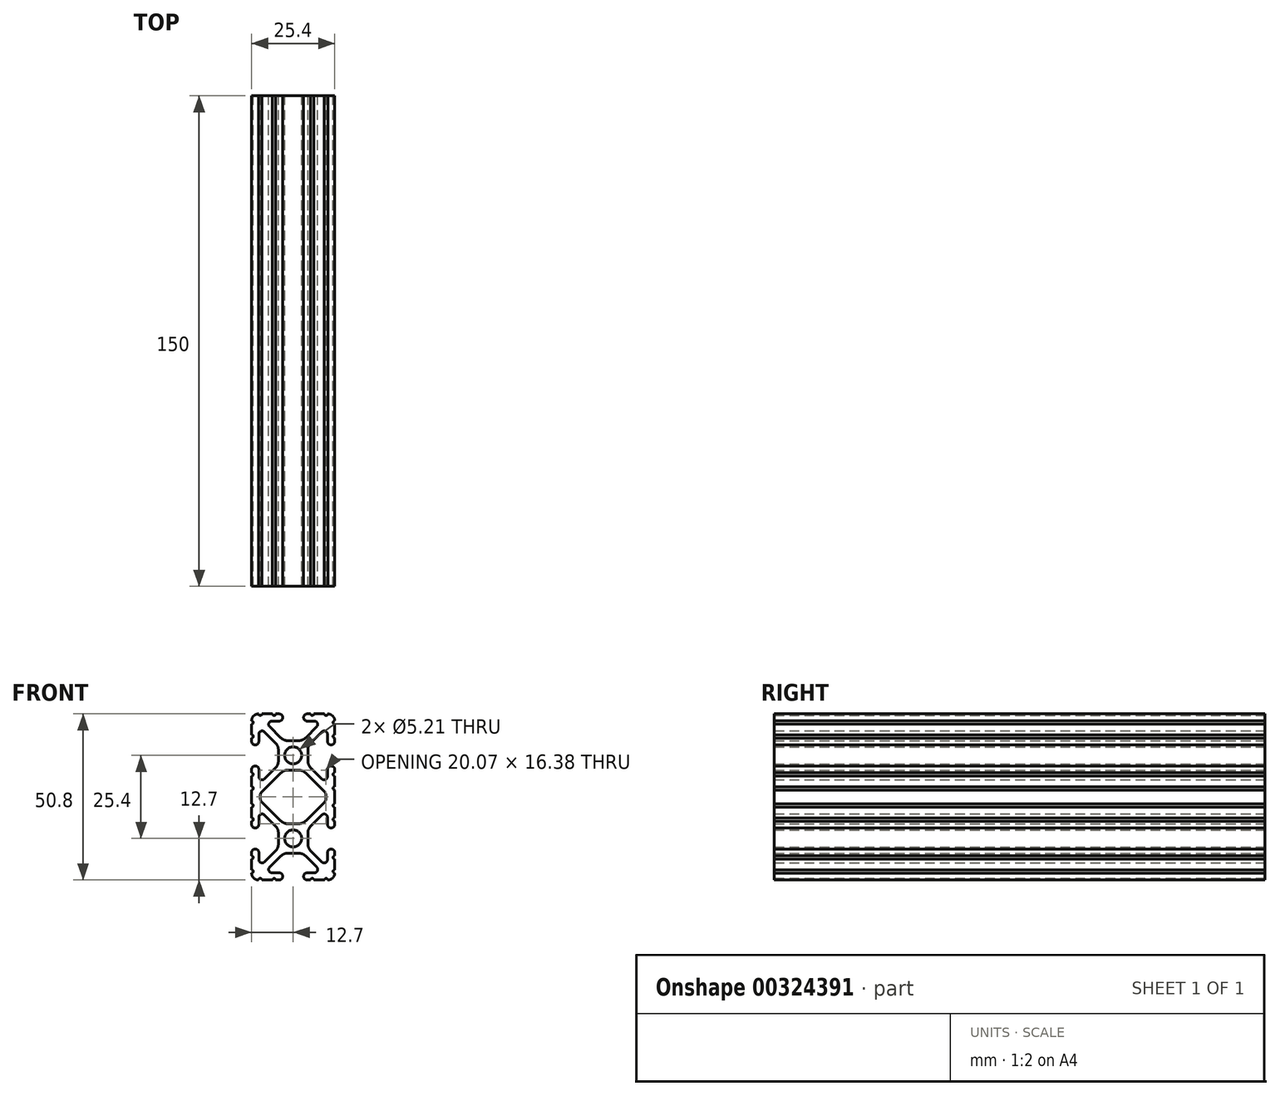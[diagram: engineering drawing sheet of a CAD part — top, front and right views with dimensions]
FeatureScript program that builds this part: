
annotation { "Feature Type Name" : "Feature", "Feature Type Description" : "" }
export const myFeature = defineFeature(function(context is Context, id is Id, definition is map)
    precondition{}
    {
        {
            var Q0;
            Q0=qCreatedBy(makeId("Front.planeOp"),FACE);
            var sketch = newSketch(context, id + "F0", { "sketchPlane" : qUnion([Q0])});
            skArc(sketch, "E0", {"start": v(2.6, -12.7) * mm, "mid": v(0, -10.1) * mm, "end": v(-2.6, -12.7) * mm});
            skArc(sketch, "E1", {"start": v(-2.6, -12.7) * mm, "mid": v(0, -15.3) * mm, "end": v(2.6, -12.7) * mm});
            skArc(sketch, "E2", {"start": v(-12.7, 22.25) * mm, "mid": v(-12.2, 22.76) * mm, "end": v(-12.7, 23.28) * mm});
            skLineSegment(sketch, "E3", {"start": v(-12.7, 22.25) * mm, "end": v(-12.7, 19.02) * mm});
            skArc(sketch, "E4", {"start": v(-12.7, 18) * mm, "mid": v(-12.2, 18.52) * mm, "end": v(-12.7, 19.02) * mm});
            skLineSegment(sketch, "E5", {"start": v(-12.7, 18) * mm, "end": v(-12.7, 17) * mm});
            skArc(sketch, "E6", {"start": v(-12.7, 17) * mm, "mid": v(-11.6, 15.9) * mm, "end": v(-10.5, 17) * mm});
            skLineSegment(sketch, "E7", {"start": v(-10.5, 17) * mm, "end": v(-10.5, 19.17) * mm});
            skArc(sketch, "E8", {"start": v(-8.76, 19.9) * mm, "mid": v(-9.86, 20.11) * mm, "end": v(-10.5, 19.17) * mm});
            skLineSegment(sketch, "E9", {"start": v(-8.76, 19.9) * mm, "end": v(-5.44, 16.58) * mm});
            skArc(sketch, "E10", {"start": v(-4.5, 14.33) * mm, "mid": v(-4.75, 15.55) * mm, "end": v(-5.44, 16.58) * mm});
            skLineSegment(sketch, "E11", {"start": v(-4.5, 14.33) * mm, "end": v(-4.5, 11.07) * mm});
            skArc(sketch, "E12", {"start": v(-5.44, 8.82) * mm, "mid": v(-4.75, 9.85) * mm, "end": v(-4.5, 11.07) * mm});
            skLineSegment(sketch, "E13", {"start": v(-5.44, 8.82) * mm, "end": v(-8.76, 5.5) * mm});
            skArc(sketch, "E14", {"start": v(-10.5, 6.23) * mm, "mid": v(-9.86, 5.29) * mm, "end": v(-8.76, 5.5) * mm});
            skLineSegment(sketch, "E15", {"start": v(-10.5, 6.23) * mm, "end": v(-10.5, 8.4) * mm});
            skArc(sketch, "E16", {"start": v(-10.5, 8.4) * mm, "mid": v(-11.6, 9.5) * mm, "end": v(-12.7, 8.4) * mm});
            skLineSegment(sketch, "E17", {"start": v(-12.7, 8.4) * mm, "end": v(-12.7, 7.4) * mm});
            skArc(sketch, "E18", {"start": v(-12.7, 6.38) * mm, "mid": v(-12.2, 6.88) * mm, "end": v(-12.7, 7.4) * mm});
            skLineSegment(sketch, "E19", {"start": v(-12.7, 6.38) * mm, "end": v(-12.7, 3.15) * mm});
            skArc(sketch, "E20", {"start": v(-12.7, 2.13) * mm, "mid": v(-12.2, 2.64) * mm, "end": v(-12.7, 3.15) * mm});
            skLineSegment(sketch, "E21", {"start": v(-12.7, 2.13) * mm, "end": v(-12.7, -2.13) * mm});
            skArc(sketch, "E22", {"start": v(-12.7, -3.15) * mm, "mid": v(-12.2, -2.64) * mm, "end": v(-12.7, -2.13) * mm});
            skLineSegment(sketch, "E23", {"start": v(-12.7, -3.15) * mm, "end": v(-12.7, -6.38) * mm});
            skArc(sketch, "E24", {"start": v(-12.7, -7.4) * mm, "mid": v(-12.2, -6.88) * mm, "end": v(-12.7, -6.38) * mm});
            skLineSegment(sketch, "E25", {"start": v(-12.7, -7.4) * mm, "end": v(-12.7, -8.4) * mm});
            skArc(sketch, "E26", {"start": v(-12.7, -8.4) * mm, "mid": v(-11.6, -9.5) * mm, "end": v(-10.5, -8.4) * mm});
            skLineSegment(sketch, "E27", {"start": v(-10.5, -8.4) * mm, "end": v(-10.5, -6.23) * mm});
            skArc(sketch, "E28", {"start": v(-8.76, -5.5) * mm, "mid": v(-9.86, -5.29) * mm, "end": v(-10.5, -6.23) * mm});
            skLineSegment(sketch, "E29", {"start": v(-8.76, -5.5) * mm, "end": v(-5.44, -8.82) * mm});
            skArc(sketch, "E30", {"start": v(-4.5, -11.07) * mm, "mid": v(-4.75, -9.85) * mm, "end": v(-5.44, -8.82) * mm});
            skLineSegment(sketch, "E31", {"start": v(-4.5, -11.07) * mm, "end": v(-4.5, -14.33) * mm});
            skArc(sketch, "E32", {"start": v(-5.44, -16.58) * mm, "mid": v(-4.75, -15.55) * mm, "end": v(-4.5, -14.33) * mm});
            skLineSegment(sketch, "E33", {"start": v(-5.44, -16.58) * mm, "end": v(-8.76, -19.9) * mm});
            skArc(sketch, "E34", {"start": v(-10.5, -19.17) * mm, "mid": v(-9.86, -20.11) * mm, "end": v(-8.76, -19.9) * mm});
            skLineSegment(sketch, "E35", {"start": v(-10.5, -19.17) * mm, "end": v(-10.5, -17) * mm});
            skArc(sketch, "E36", {"start": v(-10.5, -17) * mm, "mid": v(-11.6, -15.9) * mm, "end": v(-12.7, -17) * mm});
            skLineSegment(sketch, "E37", {"start": v(-12.7, -17) * mm, "end": v(-12.7, -18) * mm});
            skArc(sketch, "E38", {"start": v(-12.7, -19.02) * mm, "mid": v(-12.2, -18.52) * mm, "end": v(-12.7, -18) * mm});
            skLineSegment(sketch, "E39", {"start": v(-12.7, -19.02) * mm, "end": v(-12.7, -22.25) * mm});
            skArc(sketch, "E40", {"start": v(-12.7, -23.28) * mm, "mid": v(-12.2, -22.76) * mm, "end": v(-12.7, -22.25) * mm});
            skArc(sketch, "E41", {"start": v(-12.7, -23.28) * mm, "mid": v(-12.08, -24.78) * mm, "end": v(-10.58, -25.4) * mm});
            skArc(sketch, "E42", {"start": v(-9.55, -25.4) * mm, "mid": v(-10.06, -24.9) * mm, "end": v(-10.58, -25.4) * mm});
            skLineSegment(sketch, "E43", {"start": v(-9.55, -25.4) * mm, "end": v(-6.32, -25.4) * mm});
            skArc(sketch, "E44", {"start": v(-5.3, -25.4) * mm, "mid": v(-5.82, -24.9) * mm, "end": v(-6.32, -25.4) * mm});
            skLineSegment(sketch, "E45", {"start": v(-5.3, -25.4) * mm, "end": v(-4.3, -25.4) * mm});
            skArc(sketch, "E46", {"start": v(-4.3, -25.4) * mm, "mid": v(-3.2, -24.3) * mm, "end": v(-4.3, -23.2) * mm});
            skLineSegment(sketch, "E47", {"start": v(-4.3, -23.2) * mm, "end": v(-6.47, -23.2) * mm});
            skArc(sketch, "E48", {"start": v(-7.2, -21.46) * mm, "mid": v(-7.41, -22.56) * mm, "end": v(-6.47, -23.2) * mm});
            skLineSegment(sketch, "E49", {"start": v(-7.2, -21.46) * mm, "end": v(-3.88, -18.14) * mm});
            skArc(sketch, "E50", {"start": v(-1.63, -17.2) * mm, "mid": v(-2.85, -17.45) * mm, "end": v(-3.88, -18.14) * mm});
            skLineSegment(sketch, "E51", {"start": v(-1.63, -17.2) * mm, "end": v(1.63, -17.2) * mm});
            skArc(sketch, "E52", {"start": v(3.88, -18.14) * mm, "mid": v(2.85, -17.45) * mm, "end": v(1.63, -17.2) * mm});
            skLineSegment(sketch, "E53", {"start": v(3.88, -18.14) * mm, "end": v(7.2, -21.46) * mm});
            skArc(sketch, "E54", {"start": v(6.47, -23.2) * mm, "mid": v(7.41, -22.56) * mm, "end": v(7.2, -21.46) * mm});
            skLineSegment(sketch, "E55", {"start": v(6.47, -23.2) * mm, "end": v(4.3, -23.2) * mm});
            skArc(sketch, "E56", {"start": v(4.3, -23.2) * mm, "mid": v(3.2, -24.3) * mm, "end": v(4.3, -25.4) * mm});
            skLineSegment(sketch, "E57", {"start": v(4.3, -25.4) * mm, "end": v(5.3, -25.4) * mm});
            skArc(sketch, "E58", {"start": v(6.32, -25.4) * mm, "mid": v(5.82, -24.9) * mm, "end": v(5.3, -25.4) * mm});
            skLineSegment(sketch, "E59", {"start": v(6.32, -25.4) * mm, "end": v(9.55, -25.4) * mm});
            skArc(sketch, "E60", {"start": v(10.58, -25.4) * mm, "mid": v(10.06, -24.9) * mm, "end": v(9.55, -25.4) * mm});
            skArc(sketch, "E61", {"start": v(10.58, -25.4) * mm, "mid": v(12.08, -24.78) * mm, "end": v(12.7, -23.28) * mm});
            skArc(sketch, "E62", {"start": v(12.7, -22.25) * mm, "mid": v(12.2, -22.76) * mm, "end": v(12.7, -23.28) * mm});
            skLineSegment(sketch, "E63", {"start": v(12.7, -22.25) * mm, "end": v(12.7, -19.02) * mm});
            skArc(sketch, "E64", {"start": v(12.7, -18) * mm, "mid": v(12.2, -18.52) * mm, "end": v(12.7, -19.02) * mm});
            skLineSegment(sketch, "E65", {"start": v(12.7, -18) * mm, "end": v(12.7, -17) * mm});
            skArc(sketch, "E66", {"start": v(12.7, -17) * mm, "mid": v(11.6, -15.9) * mm, "end": v(10.5, -17) * mm});
            skLineSegment(sketch, "E67", {"start": v(10.5, -17) * mm, "end": v(10.5, -19.17) * mm});
            skArc(sketch, "E68", {"start": v(8.76, -19.9) * mm, "mid": v(9.86, -20.11) * mm, "end": v(10.5, -19.17) * mm});
            skLineSegment(sketch, "E69", {"start": v(8.76, -19.9) * mm, "end": v(5.44, -16.58) * mm});
            skArc(sketch, "E70", {"start": v(4.5, -14.33) * mm, "mid": v(4.75, -15.55) * mm, "end": v(5.44, -16.58) * mm});
            skLineSegment(sketch, "E71", {"start": v(4.5, -14.33) * mm, "end": v(4.5, -11.07) * mm});
            skArc(sketch, "E72", {"start": v(5.44, -8.82) * mm, "mid": v(4.75, -9.85) * mm, "end": v(4.5, -11.07) * mm});
            skLineSegment(sketch, "E73", {"start": v(5.44, -8.82) * mm, "end": v(8.76, -5.5) * mm});
            skArc(sketch, "E74", {"start": v(10.5, -6.23) * mm, "mid": v(9.86, -5.29) * mm, "end": v(8.76, -5.5) * mm});
            skLineSegment(sketch, "E75", {"start": v(10.5, -6.23) * mm, "end": v(10.5, -8.4) * mm});
            skArc(sketch, "E76", {"start": v(10.5, -8.4) * mm, "mid": v(11.6, -9.5) * mm, "end": v(12.7, -8.4) * mm});
            skLineSegment(sketch, "E77", {"start": v(12.7, -8.4) * mm, "end": v(12.7, -7.4) * mm});
            skArc(sketch, "E78", {"start": v(12.7, -6.38) * mm, "mid": v(12.2, -6.88) * mm, "end": v(12.7, -7.4) * mm});
            skLineSegment(sketch, "E79", {"start": v(12.7, -6.38) * mm, "end": v(12.7, -3.15) * mm});
            skArc(sketch, "E80", {"start": v(12.7, -2.13) * mm, "mid": v(12.2, -2.64) * mm, "end": v(12.7, -3.15) * mm});
            skLineSegment(sketch, "E81", {"start": v(12.7, -2.13) * mm, "end": v(12.7, 2.13) * mm});
            skArc(sketch, "E82", {"start": v(12.7, 3.15) * mm, "mid": v(12.2, 2.64) * mm, "end": v(12.7, 2.13) * mm});
            skLineSegment(sketch, "E83", {"start": v(12.7, 3.15) * mm, "end": v(12.7, 6.38) * mm});
            skArc(sketch, "E84", {"start": v(12.7, 7.4) * mm, "mid": v(12.2, 6.88) * mm, "end": v(12.7, 6.38) * mm});
            skLineSegment(sketch, "E85", {"start": v(12.7, 7.4) * mm, "end": v(12.7, 8.4) * mm});
            skArc(sketch, "E86", {"start": v(12.7, 8.4) * mm, "mid": v(11.6, 9.5) * mm, "end": v(10.5, 8.4) * mm});
            skLineSegment(sketch, "E87", {"start": v(10.5, 8.4) * mm, "end": v(10.5, 6.23) * mm});
            skArc(sketch, "E88", {"start": v(8.76, 5.5) * mm, "mid": v(9.86, 5.29) * mm, "end": v(10.5, 6.23) * mm});
            skLineSegment(sketch, "E89", {"start": v(8.76, 5.5) * mm, "end": v(5.44, 8.82) * mm});
            skArc(sketch, "E90", {"start": v(4.5, 11.07) * mm, "mid": v(4.75, 9.85) * mm, "end": v(5.44, 8.82) * mm});
            skLineSegment(sketch, "E91", {"start": v(4.5, 11.07) * mm, "end": v(4.5, 14.33) * mm});
            skArc(sketch, "E92", {"start": v(5.44, 16.58) * mm, "mid": v(4.75, 15.55) * mm, "end": v(4.5, 14.33) * mm});
            skLineSegment(sketch, "E93", {"start": v(5.44, 16.58) * mm, "end": v(8.76, 19.9) * mm});
            skArc(sketch, "E94", {"start": v(10.5, 19.17) * mm, "mid": v(9.86, 20.11) * mm, "end": v(8.76, 19.9) * mm});
            skLineSegment(sketch, "E95", {"start": v(10.5, 19.17) * mm, "end": v(10.5, 17) * mm});
            skArc(sketch, "E96", {"start": v(10.5, 17) * mm, "mid": v(11.6, 15.9) * mm, "end": v(12.7, 17) * mm});
            skLineSegment(sketch, "E97", {"start": v(12.7, 17) * mm, "end": v(12.7, 18) * mm});
            skArc(sketch, "E98", {"start": v(12.7, 19.02) * mm, "mid": v(12.2, 18.52) * mm, "end": v(12.7, 18) * mm});
            skLineSegment(sketch, "E99", {"start": v(12.7, 19.02) * mm, "end": v(12.7, 22.25) * mm});
            skArc(sketch, "E100", {"start": v(12.7, 23.28) * mm, "mid": v(12.2, 22.76) * mm, "end": v(12.7, 22.25) * mm});
            skArc(sketch, "E101", {"start": v(12.7, 23.28) * mm, "mid": v(12.08, 24.78) * mm, "end": v(10.58, 25.4) * mm});
            skArc(sketch, "E102", {"start": v(9.55, 25.4) * mm, "mid": v(10.06, 24.9) * mm, "end": v(10.58, 25.4) * mm});
            skLineSegment(sketch, "E103", {"start": v(9.55, 25.4) * mm, "end": v(6.32, 25.4) * mm});
            skArc(sketch, "E104", {"start": v(5.3, 25.4) * mm, "mid": v(5.82, 24.9) * mm, "end": v(6.32, 25.4) * mm});
            skLineSegment(sketch, "E105", {"start": v(5.3, 25.4) * mm, "end": v(4.3, 25.4) * mm});
            skArc(sketch, "E106", {"start": v(4.3, 25.4) * mm, "mid": v(3.2, 24.3) * mm, "end": v(4.3, 23.2) * mm});
            skLineSegment(sketch, "E107", {"start": v(4.3, 23.2) * mm, "end": v(6.47, 23.2) * mm});
            skArc(sketch, "E108", {"start": v(7.2, 21.46) * mm, "mid": v(7.41, 22.56) * mm, "end": v(6.47, 23.2) * mm});
            skLineSegment(sketch, "E109", {"start": v(7.2, 21.46) * mm, "end": v(3.88, 18.14) * mm});
            skArc(sketch, "E110", {"start": v(1.63, 17.2) * mm, "mid": v(2.85, 17.45) * mm, "end": v(3.88, 18.14) * mm});
            skLineSegment(sketch, "E111", {"start": v(1.63, 17.2) * mm, "end": v(-1.63, 17.2) * mm});
            skArc(sketch, "E112", {"start": v(-3.88, 18.14) * mm, "mid": v(-2.85, 17.45) * mm, "end": v(-1.63, 17.2) * mm});
            skLineSegment(sketch, "E113", {"start": v(-3.88, 18.14) * mm, "end": v(-7.2, 21.46) * mm});
            skArc(sketch, "E114", {"start": v(-6.47, 23.2) * mm, "mid": v(-7.41, 22.56) * mm, "end": v(-7.2, 21.46) * mm});
            skLineSegment(sketch, "E115", {"start": v(-6.47, 23.2) * mm, "end": v(-4.3, 23.2) * mm});
            skArc(sketch, "E116", {"start": v(-4.3, 23.2) * mm, "mid": v(-3.2, 24.3) * mm, "end": v(-4.3, 25.4) * mm});
            skLineSegment(sketch, "E117", {"start": v(-4.3, 25.4) * mm, "end": v(-5.3, 25.4) * mm});
            skArc(sketch, "E118", {"start": v(-6.32, 25.4) * mm, "mid": v(-5.82, 24.9) * mm, "end": v(-5.3, 25.4) * mm});
            skLineSegment(sketch, "E119", {"start": v(-6.32, 25.4) * mm, "end": v(-9.55, 25.4) * mm});
            skArc(sketch, "E120", {"start": v(-10.58, 25.4) * mm, "mid": v(-10.06, 24.9) * mm, "end": v(-9.55, 25.4) * mm});
            skArc(sketch, "E121", {"start": v(-10.58, 25.4) * mm, "mid": v(-12.08, 24.78) * mm, "end": v(-12.7, 23.28) * mm});
            skArc(sketch, "E122", {"start": v(2.6, 12.7) * mm, "mid": v(0, 15.3) * mm, "end": v(-2.6, 12.7) * mm});
            skArc(sketch, "E123", {"start": v(-2.6, 12.7) * mm, "mid": v(0, 10.1) * mm, "end": v(2.6, 12.7) * mm});
            skArc(sketch, "E124", {"start": v(-9.57, 1.57) * mm, "mid": v(-9.91, 1.05) * mm, "end": v(-10.03, 0.45) * mm});
            skLineSegment(sketch, "E125", {"start": v(-3.88, 7.26) * mm, "end": v(-9.57, 1.57) * mm});
            skArc(sketch, "E126", {"start": v(-1.63, 8.2) * mm, "mid": v(-2.85, 7.95) * mm, "end": v(-3.88, 7.26) * mm});
            skLineSegment(sketch, "E127", {"start": v(1.63, 8.2) * mm, "end": v(-1.63, 8.2) * mm});
            skArc(sketch, "E128", {"start": v(3.88, 7.26) * mm, "mid": v(2.85, 7.95) * mm, "end": v(1.63, 8.2) * mm});
            skLineSegment(sketch, "E129", {"start": v(9.57, 1.57) * mm, "end": v(3.88, 7.26) * mm});
            skArc(sketch, "E130", {"start": v(10.03, 0.45) * mm, "mid": v(9.91, 1.05) * mm, "end": v(9.57, 1.57) * mm});
            skLineSegment(sketch, "E131", {"start": v(10.03, -0.45) * mm, "end": v(10.03, 0.45) * mm});
            skArc(sketch, "E132", {"start": v(9.57, -1.57) * mm, "mid": v(9.91, -1.05) * mm, "end": v(10.03, -0.45) * mm});
            skLineSegment(sketch, "E133", {"start": v(3.88, -7.26) * mm, "end": v(9.57, -1.57) * mm});
            skArc(sketch, "E134", {"start": v(1.63, -8.2) * mm, "mid": v(2.85, -7.95) * mm, "end": v(3.88, -7.26) * mm});
            skLineSegment(sketch, "E135", {"start": v(-1.63, -8.2) * mm, "end": v(1.63, -8.2) * mm});
            skArc(sketch, "E136", {"start": v(-3.88, -7.26) * mm, "mid": v(-2.85, -7.95) * mm, "end": v(-1.63, -8.2) * mm});
            skLineSegment(sketch, "E137", {"start": v(-9.57, -1.57) * mm, "end": v(-3.88, -7.26) * mm});
            skArc(sketch, "E138", {"start": v(-10.03, -0.45) * mm, "mid": v(-9.91, -1.05) * mm, "end": v(-9.57, -1.57) * mm});
            skLineSegment(sketch, "E139", {"start": v(-10.03, 0.45) * mm, "end": v(-10.03, -0.45) * mm});
            skSolve(sketch);
        }
        {
            var Q0;
            Q0=makeQuery(id+"F0.imprint","IMPRINT",FACE,{"disambiguationData":[TD([[makeQuery(id+"F0.imprint","IMPRINT",EDGE,{"derivedFrom":sQuery(id+"F0.wireOp",EDGE,"E0")}),-1.0]])]});
            extrude(context, id + "F1", {"entities" : qUnion([Q0]), "depth" : 150 * mm, "offsetDistance" : 25 * mm});
        }
    });
